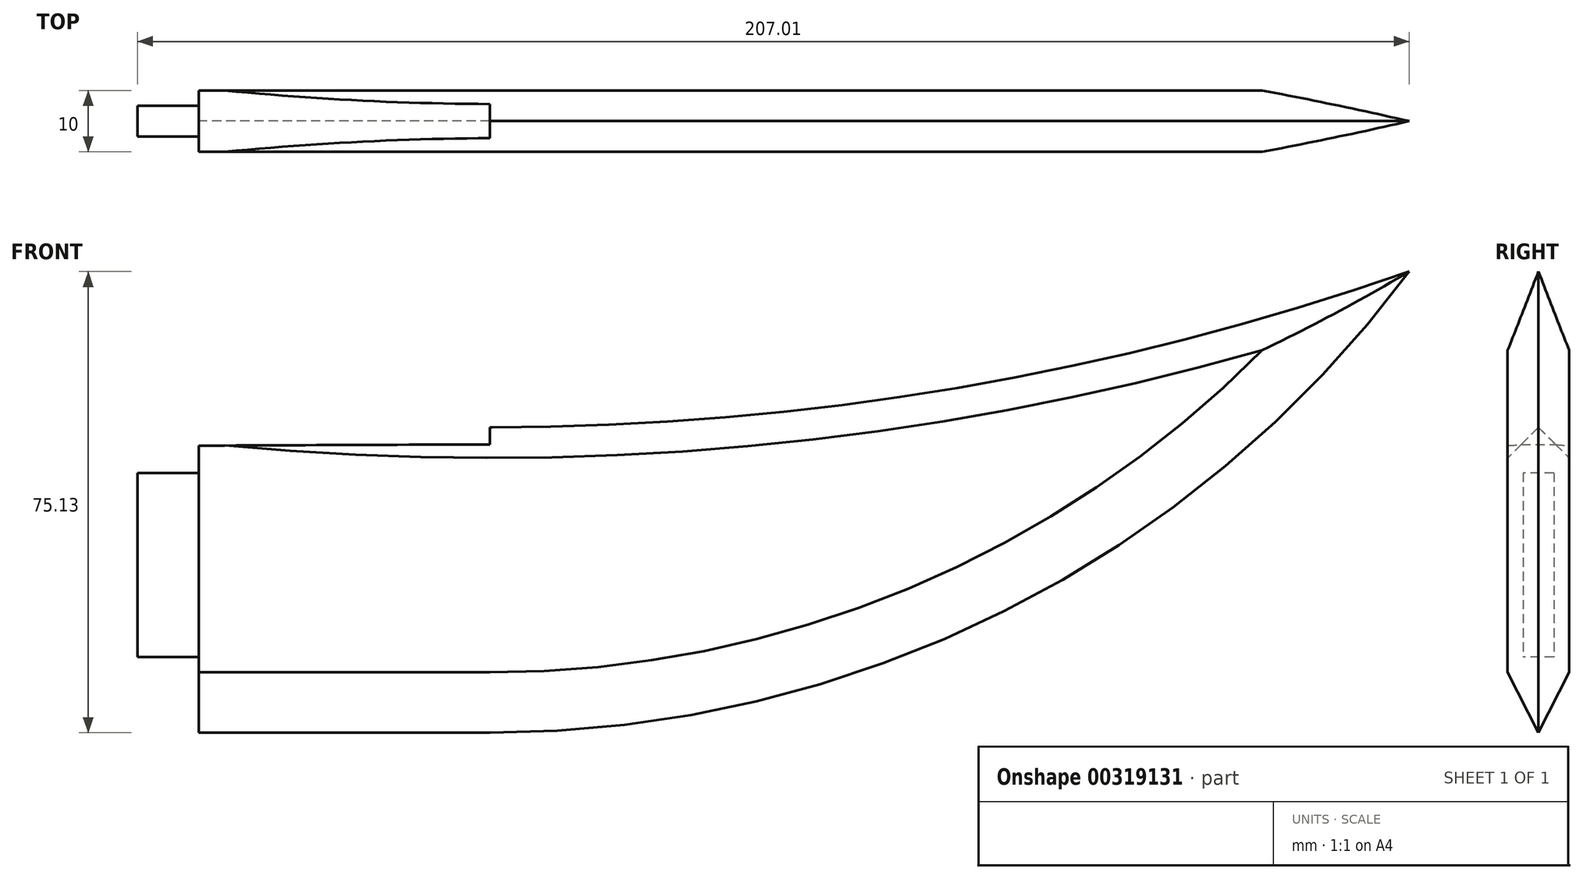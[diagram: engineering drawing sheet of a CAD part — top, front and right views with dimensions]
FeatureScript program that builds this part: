
annotation { "Feature Type Name" : "Feature", "Feature Type Description" : "" }
export const myFeature = defineFeature(function(context is Context, id is Id, definition is map)
    precondition{}
    {
        {
            var Q0;
            Q0=qCreatedBy(makeId("Front.planeOp"),FACE);
            var sketch = newSketch(context, id + "F0", { "sketchPlane" : qUnion([Q0])});
            skArc(sketch, "E0", {"start": v(50, -50) * mm, "mid": v(133.96, -30.06) * mm, "end": v(200, 25.5) * mm});
            skArc(sketch, "E1.0", {"start": v(50, -47.14) * mm, "mid": v(128.4, -29.59) * mm, "end": v(191.84, 19.71) * mm});
            skArc(sketch, "E1.1", {"start": v(50, -2.86) * mm, "mid": v(121.81, 2.82) * mm, "end": v(191.84, 19.71) * mm});
            skLineSegment(sketch, "E1.2", {"start": v(2.64, -47.14) * mm, "end": v(50, -47.14) * mm});
            skLineSegment(sketch, "E1.3", {"start": v(2.64, -3.07) * mm, "end": v(2.64, -47.14) * mm});
            skLineSegment(sketch, "E1.4", {"start": v(2.64, -3.07) * mm, "end": v(50, -2.86) * mm});
            skArc(sketch, "E2", {"start": v(200, 25.5) * mm, "mid": v(127.72, 6.7) * mm, "end": v(53.33, 0.01) * mm});
            skLineSegment(sketch, "E3", {"start": v(53.33, 0.01) * mm, "end": v(50, -2.86) * mm});
            skLineSegment(sketch, "E4", {"start": v(2.64, -47.14) * mm, "end": v(2.64, -50) * mm});
            skLineSegment(sketch, "E5", {"start": v(50, -50) * mm, "end": v(2.64, -50) * mm});
            skLineSegment(sketch, "E6", {"start": v(50, -2.86) * mm, "end": v(49.99, -0.1) * mm});
            skLineSegment(sketch, "E7", {"start": v(49.99, -0.1) * mm, "end": v(53.33, 0.01) * mm});
            skSolve(sketch);
        }
        {
            var Q0;
            Q0=makeQuery(id+"F0.imprint","IMPRINT",FACE,{"disambiguationData":[TD([[makeQuery(id+"F0.imprint","IMPRINT",EDGE,{"derivedFrom":sQuery(id+"F0.wireOp",EDGE,"E1.0")}),1.0]])]});
            extrude(context, id + "F1", {"entities" : qUnion([Q0]), "endBound" : BoundingType.SYMMETRIC, "depth" : 10 * mm});
        }
        {
            var Q0;
            Q0 = qSketchRegion(id + "F0", true);
            extrude(context, id + "F2", {"entities" : qUnion([Q0]), "operationType" : NewBodyOperationType.ADD, "endBound" : BoundingType.SYMMETRIC, "depth" : 10 * mm});
        }
        {
            var Q0;
            Q0=makeQuery(id+"F2.opExtrude","CAP_EDGE",EDGE,{"disambiguationData":[OSD([sQuery(id+"F0.wireOp",EDGE,"E2")])],"isStart":false});
            var Q1;
            Q1=makeQuery(id+"F2.opExtrude","CAP_EDGE",EDGE,{"disambiguationData":[OSD([sQuery(id+"F0.wireOp",EDGE,"E2")])],"isStart":true});
            chamfer(context, id + "F3", {"entities" : qUnion([Q0, Q1]), "width" : 5.08 * mm, "tangentPropagation" : true});
        }
        {
            var Q0;
            Q0=makeQuery(id+"F2.opExtrude","CAP_EDGE",EDGE,{"disambiguationData":[OSD([sQuery(id+"F0.wireOp",EDGE,"E0")])],"isStart":true});
            var Q1;
            Q1=makeQuery(id+"F2.opExtrude","CAP_EDGE",EDGE,{"disambiguationData":[OSD([sQuery(id+"F0.wireOp",EDGE,"E0")])],"isStart":false});
            chamfer(context, id + "F4", {"entities" : qUnion([Q0, Q1]), "chamferType" : ChamferType.TWO_OFFSETS, "width1" : 5.08 * mm, "oppositeDirection" : false, "width2" : 10 * mm, "tangentPropagation" : true});
        }
        {
            var Q0;
            {var subQ0=sQuery(id+"F0.wireOp",EDGE,"E1.3");Q0=makeQuery(id+"F2.boolean.opBoolean","MERGE",FACE,{"derivedFrom":[makeQuery(id+"F1.opExtrude","SWEPT_FACE",FACE,{"disambiguationData":[OSD([subQ0])]}),makeQuery(id+"F2.opExtrude","SWEPT_FACE",FACE,{"disambiguationData":[OSD([subQ0,sQuery(id+"F0.wireOp",EDGE,"E4")])]})]});}
            var sketch = newSketch(context, id + "F5", { "sketchPlane" : qUnion([Q0])});
            skLineSegment(sketch, "E8.bottom", {"start": v(-2.5, -7.5) * mm, "end": v(2.5, -7.5) * mm});
            skLineSegment(sketch, "E8.top", {"start": v(-2.5, -37.5) * mm, "end": v(2.5, -37.5) * mm});
            skLineSegment(sketch, "E8.left", {"start": v(-2.5, -7.5) * mm, "end": v(-2.5, -37.5) * mm});
            skLineSegment(sketch, "E8.right", {"start": v(2.5, -7.5) * mm, "end": v(2.5, -37.5) * mm});
            skLineSegment(sketch, "E9", {"start": v(-5, -3.07) * mm, "end": v(5, -3.07) * mm});
            skLineSegment(sketch, "E10", {"start": v(-5, -40) * mm, "end": v(5, -40) * mm});
            skSolve(sketch);
        }
        {
            var Q0;
            Q0=makeQuery(id+"F5.imprint","IMPRINT",FACE,{"disambiguationData":[TD([[makeQuery(id+"F5.imprint","IMPRINT",EDGE,{"derivedFrom":sQuery(id+"F5.wireOp",EDGE,"E8.bottom")}),-1.0]])]});
            extrude(context, id + "F6", {"entities" : qUnion([Q0]), "operationType" : NewBodyOperationType.ADD, "depth" : 10 * mm});
        }
    });
